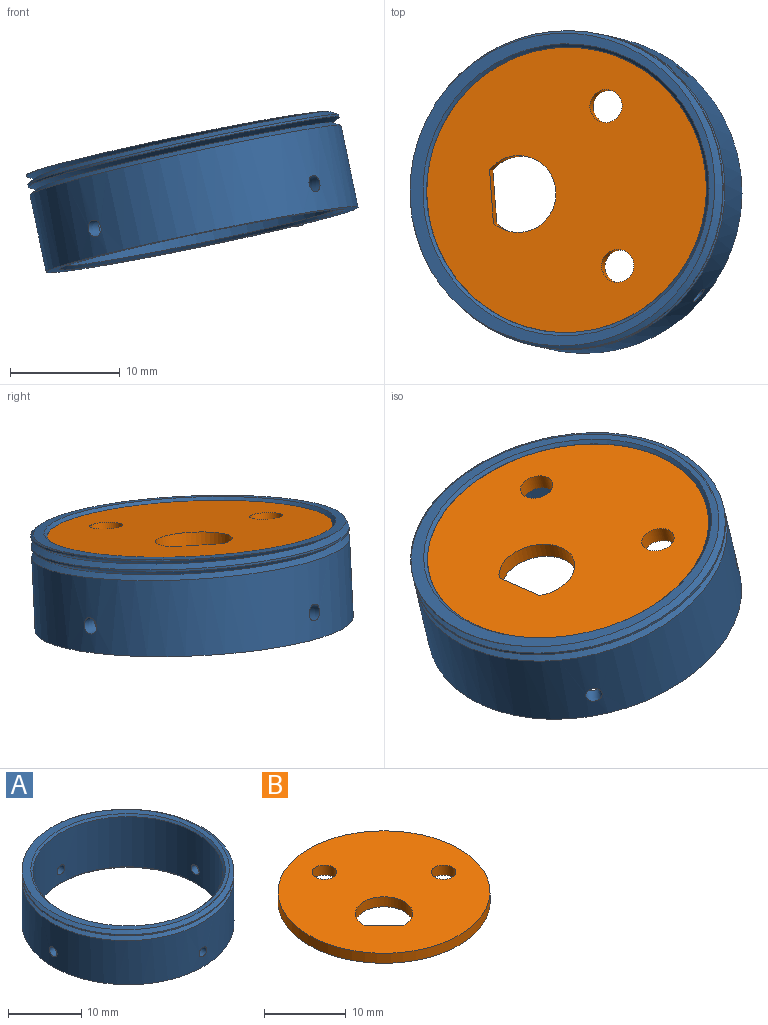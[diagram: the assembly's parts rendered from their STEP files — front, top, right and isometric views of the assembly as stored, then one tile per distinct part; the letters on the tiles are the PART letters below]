
ASSEMBLY  parts=2 mates=1
PART A: 20 faces, bbox 29.5x34x10.2 mm
  f0: plane 29x29mm, normal (0,0,-1), area 104.5mm2, adj f1,f10,f15,f16,f17,f18
  f1: cylinder r=14.5mm len=29mm, axis (0,0,-1), area 653.4mm2, adj f0,f2,f6,f7,f11,f12,f13,f14
  f2: cylinder r=14.5mm len=29mm, axis (0,0,-1), area 18.2mm2, adj f1,f3,f7,f8
  f3: cylinder r=14.5mm len=28.25mm, axis (0,0,-1), area 6.4mm2, adj f2,f5,f7,f8
  f4: cylinder r=13mm len=26mm, axis (0,0,-1), area 679.1mm2, adj f9,f10,f11,f12,f13,f14
  f5: plane 29.02x29.02mm, normal (0,0,1), area 80mm2, adj f3,f7,f8,f9
  f6: plane 0.8x0.69mm, normal (0,1,0), area 0.3mm2, adj f1,f7,f8
  f7: bspline ~33.49x29mm, area 146mm2, adj f1,f2,f3,f5,f6,f8
  f8: bspline ~33.49x29mm, area 117.3mm2, adj f2,f3,f5,f6,f7
  f9: cone r=13mm half-angle=45deg, axis (0,0,1), area 35.1mm2, adj f4,f5
  f10: cone r=13.3mm half-angle=45deg, axis (0,0,-1), area 35.1mm2, adj f0,f4
  f11: cylinder r=0.75mm len=1.5mm, axis (0,-1,0), area 7.1mm2, adj f1,f4
  f12: cylinder r=0.75mm len=1.5mm, axis (0,-1,0), area 7.1mm2, adj f1,f4
  f13: cylinder r=0.75mm len=1.5mm, axis (1,0,0), area 7.1mm2, adj f1,f4
  f14: cylinder r=0.75mm len=1.5mm, axis (1,0,0), area 7.1mm2, adj f1,f4
  f15: plane 0.42x0.1mm, normal (0,-1,0), area 0mm2, adj f0,f16,f18,f19
  f16: plane 0.78x0.1mm, normal (1,0,0), area 0.1mm2, adj f0,f15,f17,f19
  f17: plane 0.42x0.1mm, normal (0,1,0), area 0mm2, adj f0,f16,f18,f19
  f18: plane 0.78x0.1mm, normal (-1,0,0), area 0.1mm2, adj f0,f15,f17,f19
  f19: plane 0.78x0.42mm, normal (0,0,-1), area 0.3mm2, adj f15,f16,f17,f18
PART B: 7 faces, bbox 26x26x1.5 mm
  f0: plane 3.46x3.46mm, normal (0.71,0.71,0), area 7.3mm2, adj f2,f3,f4
  f1: cylinder r=13mm len=26mm, axis (0,0,-1), area 122.5mm2, adj f3,f4
  f2: cylinder r=3.5mm len=7mm, axis (0,0,-1), area 24.8mm2, adj f0,f3,f4
  f3: plane 26x26mm, normal (0,0,1), area 481.7mm2, adj f0,f1,f2,f5,f6
  f4: plane 26x26mm, normal (0,0,-1), area 481.7mm2, adj f0,f1,f2,f5,f6
  f5: cylinder r=1.5mm len=3mm, axis (0,0,-1), area 14.1mm2, adj f3,f4
  f6: cylinder r=1.5mm len=3mm, axis (0,0,-1), area 14.1mm2, adj f3,f4
PLACE A rot(axis=(-0.15,-0.19,0.97),50.9deg) t=(-0.53,-2.92,31.76)mm
PLACE B rot(axis=(0.04,-0.29,-0.96),42.1deg) t=(-1.99,-2.6,38.81)mm
MATE fastened A.f1 <-> B.f1  axis (-0.2,0.04,0.98) through (-2.29,-2.54,40.28)mm
